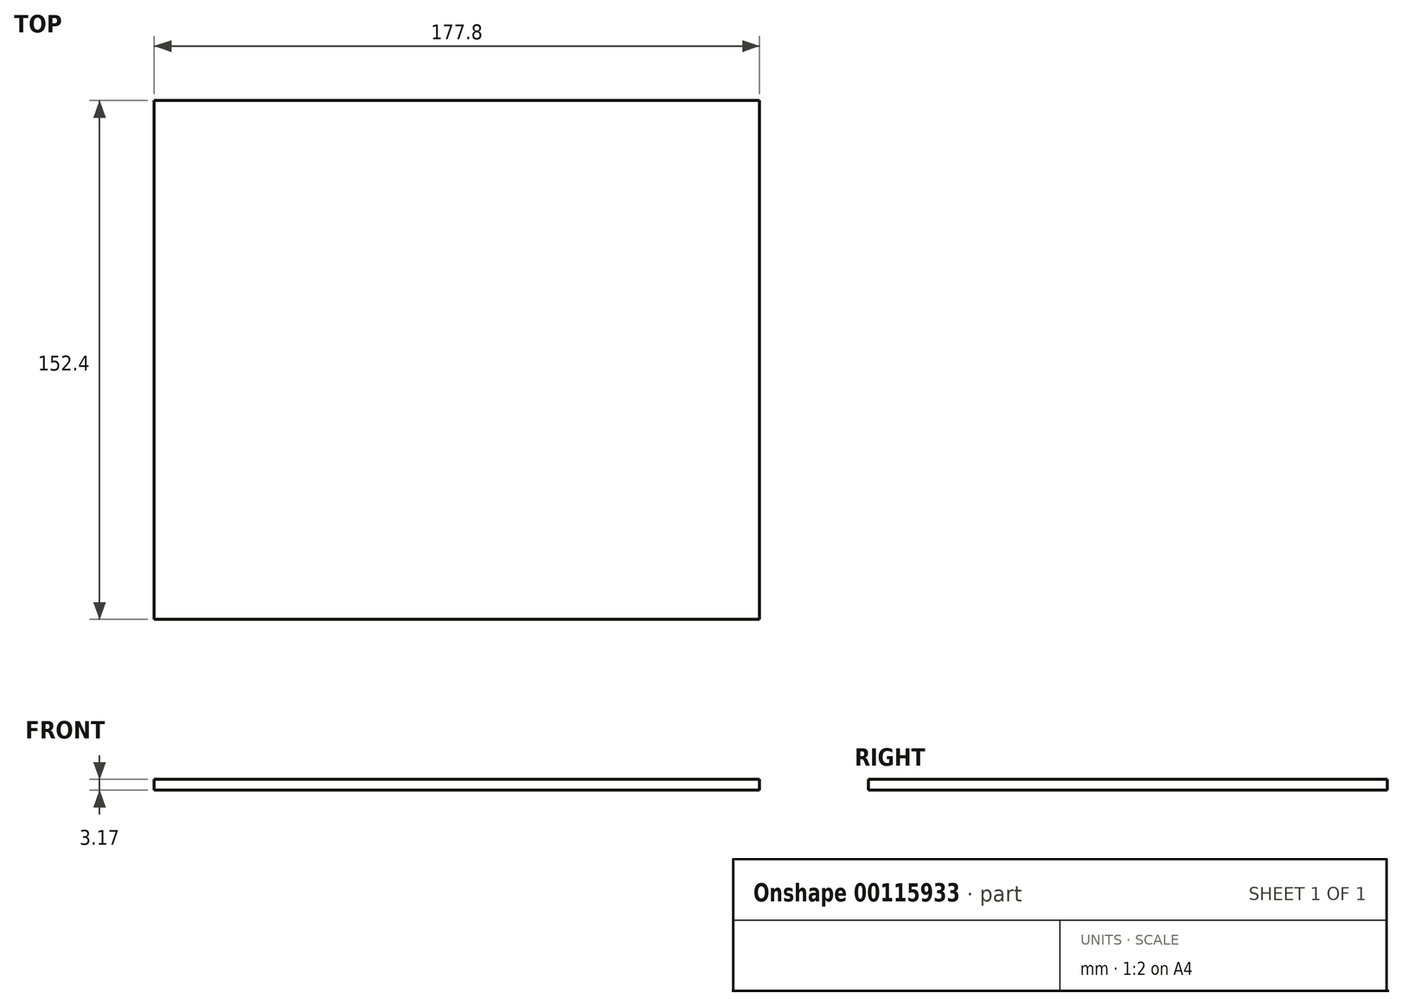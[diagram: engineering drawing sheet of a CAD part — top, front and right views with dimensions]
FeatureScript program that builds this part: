
annotation { "Feature Type Name" : "Feature", "Feature Type Description" : "" }
export const myFeature = defineFeature(function(context is Context, id is Id, definition is map)
    precondition{}
    {
        {
            var Q0;
            Q0=qCreatedBy(makeId("Top.planeOp"),FACE);
            var sketch = newSketch(context, id + "F0", { "sketchPlane" : qUnion([Q0])});
            skLineSegment(sketch, "E0.bottom", {"start": v(-105.44, 91.43) * mm, "end": v(72.36, 91.43) * mm});
            skLineSegment(sketch, "E0.top", {"start": v(-105.44, -60.97) * mm, "end": v(72.36, -60.97) * mm});
            skLineSegment(sketch, "E0.left", {"start": v(-105.44, 91.43) * mm, "end": v(-105.44, -60.97) * mm});
            skLineSegment(sketch, "E0.right", {"start": v(72.36, 91.43) * mm, "end": v(72.36, -60.97) * mm});
            skSolve(sketch);
        }
        {
            var Q0;
            Q0=makeQuery(id+"F0.imprint","IMPRINT",FACE,{"disambiguationData":[TD([[makeQuery(id+"F0.imprint","IMPRINT",EDGE,{"derivedFrom":sQuery(id+"F0.wireOp",EDGE,"E0.bottom")}),-1.0]])]});
            extrude(context, id + "F1", {"entities" : qUnion([Q0]), "depth" : 3.17 * mm});
        }
    });
